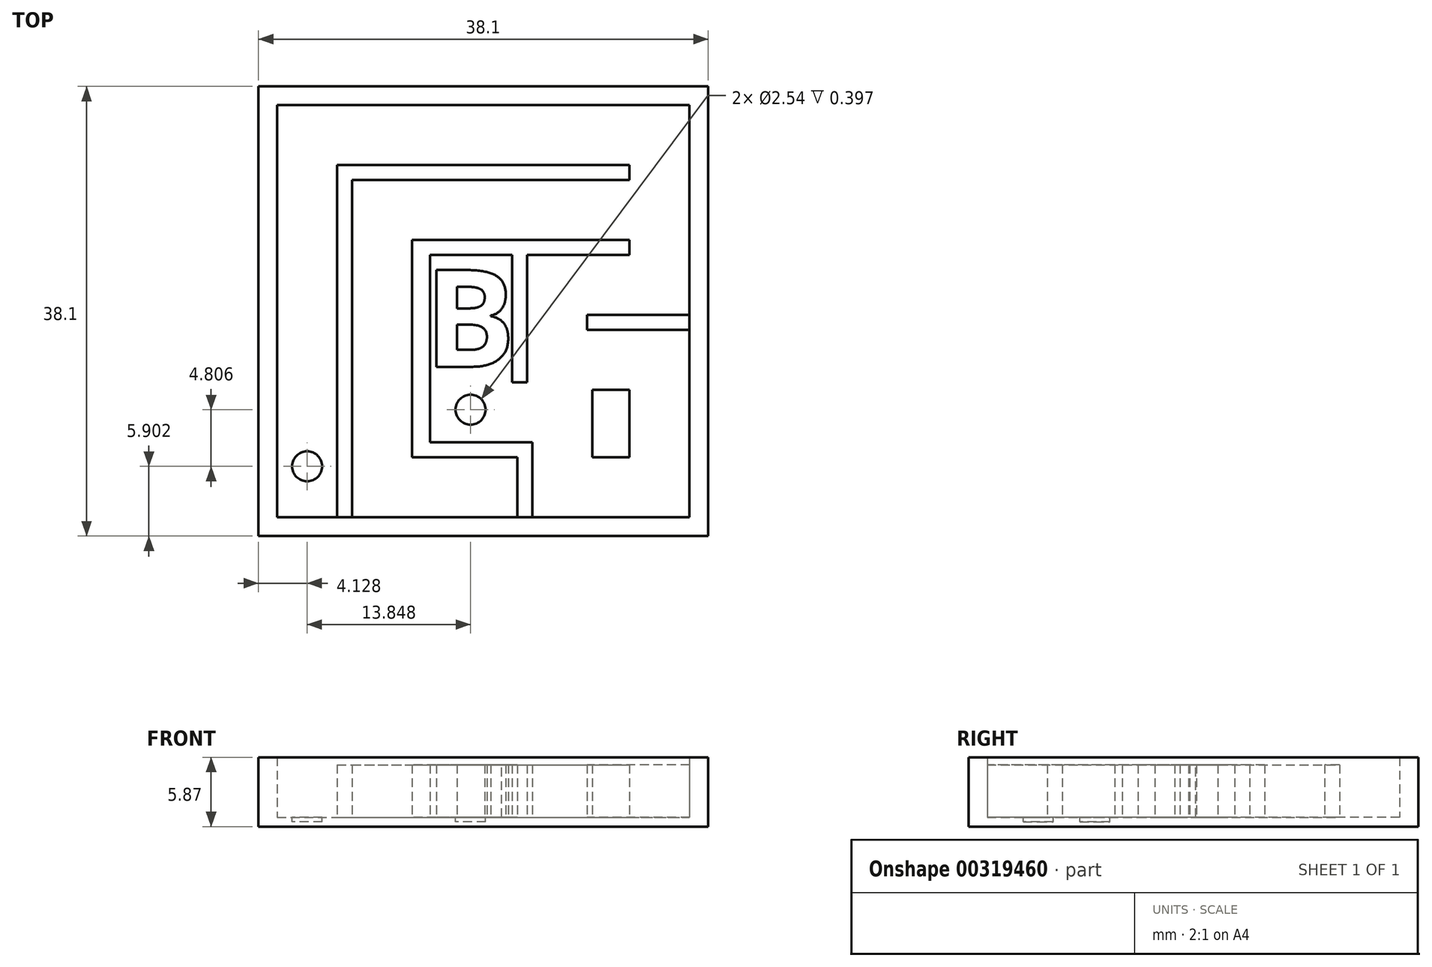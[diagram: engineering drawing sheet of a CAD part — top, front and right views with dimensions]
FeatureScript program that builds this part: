
annotation { "Feature Type Name" : "Feature", "Feature Type Description" : "" }
export const myFeature = defineFeature(function(context is Context, id is Id, definition is map)
    precondition{}
    {
        {
            var Q0;
            Q0=qCreatedBy(makeId("Top.planeOp"),FACE);
            var sketch = newSketch(context, id + "F0", { "sketchPlane" : qUnion([Q0])});
            skLineSegment(sketch, "E0.bottom", {"start": v(-23.7, 20.74) * mm, "end": v(14.4, 20.74) * mm});
            skLineSegment(sketch, "E0.top", {"start": v(-23.7, -17.36) * mm, "end": v(14.4, -17.36) * mm});
            skLineSegment(sketch, "E0.left", {"start": v(-23.7, 20.74) * mm, "end": v(-23.7, -17.36) * mm});
            skLineSegment(sketch, "E0.right", {"start": v(14.4, 20.74) * mm, "end": v(14.4, -17.36) * mm});
            skSolve(sketch);
        }
        {
            var Q0;
            Q0=makeQuery(id+"F0.imprint","IMPRINT",FACE,{"disambiguationData":[TD([[makeQuery(id+"F0.imprint","IMPRINT",EDGE,{"derivedFrom":sQuery(id+"F0.wireOp",EDGE,"E0.bottom")}),-1.0]])]});
            extrude(context, id + "F1", {"entities" : qUnion([Q0]), "depth" : 0.8 * mm});
        }
        {
            var Q0;
            Q0=makeQuery(id+"F1.opExtrude","CAP_FACE",FACE,{"disambiguationData":[OSD([sQuery(id+"F0.wireOp",EDGE,"E0.bottom"),sQuery(id+"F0.wireOp",EDGE,"E0.top"),sQuery(id+"F0.wireOp",EDGE,"E0.left"),sQuery(id+"F0.wireOp",EDGE,"E0.right")])],"isStart":false});
            var sketch = newSketch(context, id + "F2", { "sketchPlane" : qUnion([Q0])});
            skLineSegment(sketch, "E1.0", {"start": v(-22.12, 19.15) * mm, "end": v(12.8, 19.15) * mm});
            skLineSegment(sketch, "E1.1", {"start": v(-22.12, 19.15) * mm, "end": v(-22.12, -15.78) * mm});
            skLineSegment(sketch, "E1.2", {"start": v(-22.12, -15.78) * mm, "end": v(12.8, -15.78) * mm});
            skLineSegment(sketch, "E1.3", {"start": v(12.8, 19.15) * mm, "end": v(12.8, -15.78) * mm});
            skSolve(sketch);
        }
        {
            var Q0;
            Q0=makeQuery(id+"F2.imprint","IMPRINT",FACE,{"disambiguationData":[TD([[makeQuery(id+"F2.imprint","IMPRINT",EDGE,{"derivedFrom":sQuery(id+"F2.wireOp",EDGE,"E1.0")}),1.0]])]});
            extrude(context, id + "F3", {"entities" : qUnion([Q0]), "operationType" : NewBodyOperationType.ADD, "depth" : 5.08 * mm});
        }
        {
            var Q0;
            Q0=makeQuery(id+"F1.opExtrude","CAP_FACE",FACE,{"disambiguationData":[OSD([sQuery(id+"F0.wireOp",EDGE,"E0.bottom"),sQuery(id+"F0.wireOp",EDGE,"E0.top"),sQuery(id+"F0.wireOp",EDGE,"E0.left"),sQuery(id+"F0.wireOp",EDGE,"E0.right")])],"isStart":false});
            var sketch = newSketch(context, id + "F4", { "sketchPlane" : qUnion([Q0])});
            skLineSegment(sketch, "E2.bottom", {"start": v(-17.04, -15.78) * mm, "end": v(-15.77, -15.78) * mm});
            skLineSegment(sketch, "E2.top", {"start": v(-17.04, 14.07) * mm, "end": v(-15.77, 14.07) * mm});
            skLineSegment(sketch, "E2.left", {"start": v(-17.04, -15.78) * mm, "end": v(-17.04, 14.07) * mm});
            skLineSegment(sketch, "E2.right", {"start": v(-15.77, -15.78) * mm, "end": v(-15.77, 12.8) * mm});
            skLineSegment(sketch, "E3.bottom", {"start": v(-10.7, 14.07) * mm, "end": v(7.72, 14.07) * mm});
            skLineSegment(sketch, "E3.top", {"start": v(-9.18, 12.8) * mm, "end": v(7.72, 12.8) * mm});
            skLineSegment(sketch, "E3.right", {"start": v(7.72, 14.07) * mm, "end": v(7.72, 12.8) * mm});
            skLineSegment(sketch, "E4.bottom", {"start": v(-9.18, 7.72) * mm, "end": v(7.72, 7.72) * mm});
            skLineSegment(sketch, "E4.top", {"start": v(-9.18, 6.45) * mm, "end": v(-2.23, 6.45) * mm});
            skLineSegment(sketch, "E4.right", {"start": v(7.72, 7.72) * mm, "end": v(7.72, 6.45) * mm});
            skLineSegment(sketch, "E5.top", {"start": v(-2.23, -4.35) * mm, "end": v(-0.96, -4.35) * mm});
            skLineSegment(sketch, "E5.left", {"start": v(-2.23, 6.45) * mm, "end": v(-2.23, -4.35) * mm});
            skLineSegment(sketch, "E5.right", {"start": v(-0.96, 6.45) * mm, "end": v(-0.96, -4.35) * mm});
            skLineSegment(sketch, "E6.bottom", {"start": v(12.8, 1.37) * mm, "end": v(4.12, 1.37) * mm});
            skLineSegment(sketch, "E6.top", {"start": v(12.8, 0.1) * mm, "end": v(4.12, 0.1) * mm});
            skLineSegment(sketch, "E6.left", {"start": v(12.8, 1.37) * mm, "end": v(12.8, 0.1) * mm});
            skLineSegment(sketch, "E6.right", {"start": v(4.12, 1.37) * mm, "end": v(4.12, 0.1) * mm});
            skLineSegment(sketch, "E7.trimOffspring", {"start": v(-9.18, 6.45) * mm, "end": v(-9.18, -9.43) * mm});
            skLineSegment(sketch, "E8.trimOffspring", {"start": v(-0.96, 6.45) * mm, "end": v(7.72, 6.45) * mm});
            skLineSegment(sketch, "E9", {"start": v(-10.7, 7.72) * mm, "end": v(-10.7, -10.7) * mm});
            skLineSegment(sketch, "E10.bottom", {"start": v(4.58, -4.98) * mm, "end": v(7.72, -4.98) * mm});
            skLineSegment(sketch, "E10.top", {"start": v(4.58, -10.7) * mm, "end": v(7.72, -10.7) * mm});
            skLineSegment(sketch, "E10.left", {"start": v(4.58, -4.98) * mm, "end": v(4.58, -10.7) * mm});
            skLineSegment(sketch, "E10.right", {"start": v(7.72, -4.98) * mm, "end": v(7.72, -10.7) * mm});
            skLineSegment(sketch, "E11.top", {"start": v(-9.18, -9.43) * mm, "end": v(-0.5, -9.43) * mm});
            skLineSegment(sketch, "E12.top", {"start": v(-0.5, -15.78) * mm, "end": v(-1.77, -15.78) * mm});
            skLineSegment(sketch, "E12.right", {"start": v(-1.77, -10.7) * mm, "end": v(-1.77, -15.78) * mm});
            skLineSegment(sketch, "E13", {"start": v(-1.77, -10.7) * mm, "end": v(-10.7, -10.7) * mm});
            skLineSegment(sketch, "E14", {"start": v(-0.5, -9.43) * mm, "end": v(-0.5, -15.78) * mm});
            skText(sketch, "E15", { "text": "B", "fontName": "OpenSans-Bold.ttf"});
            skLineSegment(sketch, "E16.top", {"start": v(-9.18, 14.07) * mm, "end": v(-15.77, 14.07) * mm});
            skLineSegment(sketch, "E17", {"start": v(-15.77, 12.8) * mm, "end": v(-9.18, 12.8) * mm});
            skLineSegment(sketch, "E18", {"start": v(-9.18, 7.72) * mm, "end": v(-10.7, 7.72) * mm});
            skLineSegment(sketch, "E19", {"start": v(-22.12, -15.78) * mm, "end": v(-17.04, -15.78) * mm});
            skCircle(sketch, "E20", {"center": v(-19.58, -11.46) * mm, "radius": 1.27 * mm});
            skPoint(sketch, "E20.centerSnap0", {"position": v(-19.58, -15.78) * mm});
            skCircle(sketch, "E21", {"center": v(-5.73, -6.65) * mm, "radius": 1.27 * mm});
            const initialGuessF4  = {"E15": [-0.00966, -0.00302, 1, 0, 0.00827]};
            skSetInitialGuess(sketch, initialGuessF4);
            skSolve(sketch);
        }
        {
            var Q0;
            Q0=makeQuery(id+"F4.imprint","IMPRINT",FACE,{"disambiguationData":[TD([[makeQuery(id+"F4.imprint","IMPRINT",EDGE,{"derivedFrom":sQuery(id+"F4.wireOp",EDGE,"E2.bottom")}),1.0]])]});
            var Q1;
            Q1=makeQuery(id+"F4.imprint","IMPRINT",FACE,{"disambiguationData":[TD([[makeQuery(id+"F4.imprint","IMPRINT",EDGE,{"derivedFrom":sQuery(id+"F4.wireOp",EDGE,"E4.bottom")}),-1.0]])]});
            var Q2;
            Q2=makeQuery(id+"F4.imprint","IMPRINT",FACE,{"disambiguationData":[TD([[makeQuery(id+"F4.imprint","IMPRINT",EDGE,{"derivedFrom":sQuery(id+"F4.wireOp",EDGE,"E15.sketch_text.stroke-0")}),-1.0]])]});
            var Q3;
            Q3=makeQuery(id+"F4.imprint","IMPRINT",FACE,{"disambiguationData":[TD([[makeQuery(id+"F4.imprint","IMPRINT",EDGE,{"derivedFrom":sQuery(id+"F4.wireOp",EDGE,"E6.bottom")}),1.0]])]});
            var Q4;
            Q4=makeQuery(id+"F4.imprint","IMPRINT",FACE,{"disambiguationData":[TD([[makeQuery(id+"F4.imprint","IMPRINT",EDGE,{"derivedFrom":sQuery(id+"F4.wireOp",EDGE,"E10.bottom")}),-1.0]])]});
            extrude(context, id + "F5", {"entities" : qUnion([Q0, Q1, Q2, Q3, Q4]), "operationType" : NewBodyOperationType.ADD, "depth" : 4.44 * mm});
        }
        {
            var Q0;
            Q0=makeQuery(id+"F4.imprint","IMPRINT",FACE,{"disambiguationData":[TD([[makeQuery(id+"F4.imprint","IMPRINT",EDGE,{"derivedFrom":sQuery(id+"F4.wireOp",EDGE,"E20")}),1.0]])]});
            var Q1;
            Q1=makeQuery(id+"F4.imprint","IMPRINT",FACE,{"disambiguationData":[TD([[makeQuery(id+"F4.imprint","IMPRINT",EDGE,{"derivedFrom":sQuery(id+"F4.wireOp",EDGE,"E21")}),1.0]])]});
            extrude(context, id + "F6", {"entities" : qUnion([Q0, Q1]), "operationType" : NewBodyOperationType.REMOVE, "oppositeDirection" : true, "depth" : 0.4 * mm});
        }
    });
